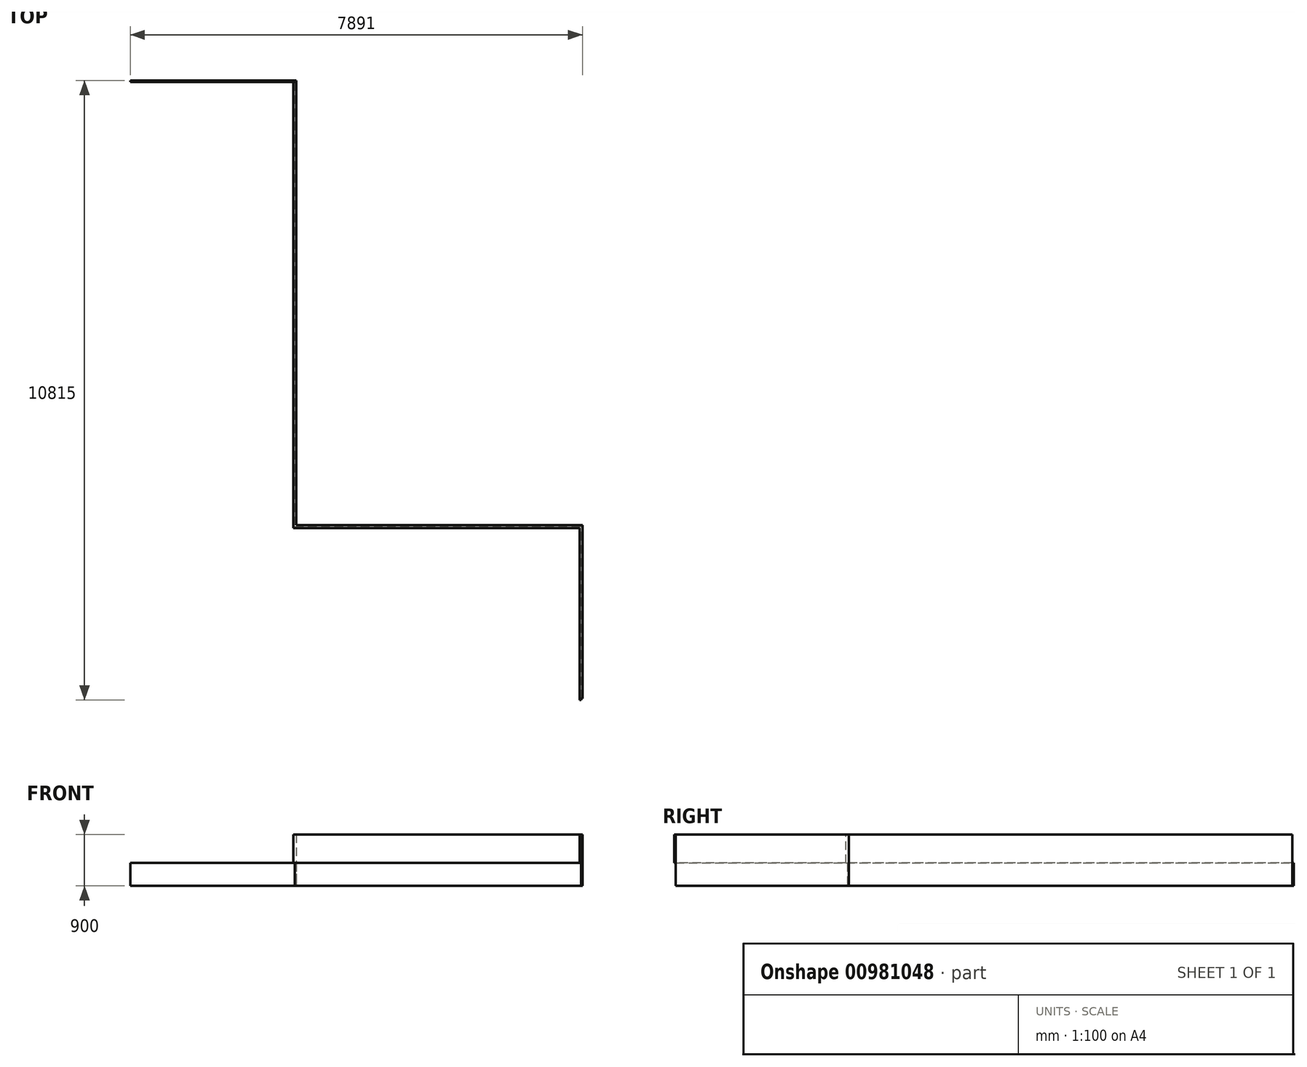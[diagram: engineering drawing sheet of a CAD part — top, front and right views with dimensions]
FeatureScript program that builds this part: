
annotation { "Feature Type Name" : "Feature", "Feature Type Description" : "" }
export const myFeature = defineFeature(function(context is Context, id is Id, definition is map)
    precondition{}
    {
        {
            var Q0;
            Q0=qCreatedBy(makeId("Front.planeOp"),FACE);
            var sketch = newSketch(context, id + "F0", { "sketchPlane" : qUnion([Q0])});
            skLineSegment(sketch, "E0.bottom", {"start": v(-6129.53, 738.4) * mm, "end": v(-1135.53, 738.4) * mm});
            skLineSegment(sketch, "E0.top", {"start": v(-6129.53, 338.4) * mm, "end": v(-1135.53, 338.4) * mm});
            skLineSegment(sketch, "E0.left", {"start": v(-6129.53, 738.4) * mm, "end": v(-6129.53, 338.4) * mm});
            skLineSegment(sketch, "E0.right", {"start": v(-1135.53, 738.4) * mm, "end": v(-1135.53, 338.4) * mm});
            skLineSegment(sketch, "E1.bottom", {"start": v(-6154.53, 738.4) * mm, "end": v(-1135.53, 738.4) * mm});
            skLineSegment(sketch, "E1.top", {"start": v(-6154.53, 1238.4) * mm, "end": v(-1135.53, 1238.4) * mm});
            skLineSegment(sketch, "E1.left", {"start": v(-6154.53, 738.4) * mm, "end": v(-6154.53, 1238.4) * mm});
            skLineSegment(sketch, "E1.right", {"start": v(-1135.53, 738.4) * mm, "end": v(-1135.53, 1238.4) * mm});
            skSolve(sketch);
        }
        {
            var Q0;
            Q0=makeQuery(id+"F0.imprint","IMPRINT",FACE,{"disambiguationData":[TD([[makeQuery(id+"F0.imprint","IMPRINT",EDGE,{"derivedFrom":sQuery(id+"F0.wireOp",EDGE,"E0.bottom")}),1.0]])]});
            extrude(context, id + "F1", {"entities" : qUnion([Q0]), "depth" : 25 * mm, "offsetDistance" : 25 * mm});
        }
        {
            var Q0;
            Q0=makeQuery(id+"F0.imprint","IMPRINT",FACE,{"disambiguationData":[TD([[makeQuery(id+"F0.imprint","IMPRINT",EDGE,{"derivedFrom":sQuery(id+"F0.wireOp",EDGE,"E0.bottom")}),-1.0]])]});
            var Q1;
            Q1=makeQuery(id+"F0.imprint","IMPRINT",FACE,{"disambiguationData":[TD([[makeQuery(id+"F0.imprint","IMPRINT",EDGE,{"derivedFrom":sQuery(id+"F0.wireOp",EDGE,"E0.bottom")}),1.0]])]});
            extrude(context, id + "F2", {"entities" : qUnion([Q0, Q1]), "operationType" : NewBodyOperationType.ADD, "oppositeDirection" : true, "depth" : 25 * mm, "offsetDistance" : 25 * mm});
        }
        {
            var Q0;
            {var subQ0=sQuery(id+"F0.wireOp",EDGE,"E1.right");Q0=makeQuery(id+"F2.boolean.opBoolean","MERGE",FACE,{"derivedFrom":[makeQuery(id+"F1.opExtrude","SWEPT_FACE",FACE,{"disambiguationData":[OSD([subQ0])]}),makeQuery(id+"F2.opExtrude","SWEPT_FACE",FACE,{"disambiguationData":[OSD([sQuery(id+"F0.wireOp",EDGE,"E0.right"),subQ0])]})]});}
            var sketch = newSketch(context, id + "F3", { "sketchPlane" : qUnion([Q0])});
            skLineSegment(sketch, "E2.bottom", {"start": v(25, 338.4) * mm, "end": v(-3003, 338.4) * mm});
            skLineSegment(sketch, "E2.top", {"start": v(25, 1238.4) * mm, "end": v(-3003, 1238.4) * mm});
            skLineSegment(sketch, "E2.left", {"start": v(25, 338.4) * mm, "end": v(25, 1238.4) * mm});
            skLineSegment(sketch, "E2.right", {"start": v(-3003, 338.4) * mm, "end": v(-3003, 1238.4) * mm});
            skLineSegment(sketch, "E3.bottom", {"start": v(-25, 738.4) * mm, "end": v(-3028, 738.4) * mm});
            skLineSegment(sketch, "E3.top", {"start": v(-25, 1238.4) * mm, "end": v(-3028, 1238.4) * mm});
            skLineSegment(sketch, "E3.left", {"start": v(-25, 738.4) * mm, "end": v(-25, 1238.4) * mm});
            skLineSegment(sketch, "E3.right", {"start": v(-3028, 738.4) * mm, "end": v(-3028, 1238.4) * mm});
            skSolve(sketch);
        }
        {
            var Q0;
            {var subQ5=sQuery(id+"F3.wireOp",EDGE,"E3.left");Q0=makeQuery(id+"F3.imprint","IMPRINT",FACE,{"disambiguationData":[TD([[makeQuery(id+"F3.imprint","IMPRINT",EDGE,{"derivedFrom":subQ5}),1.0]])]});}
            var Q1;
            {var subQ5=sQuery(id+"F3.wireOp",EDGE,"E3.right");Q1=makeQuery(id+"F3.imprint","IMPRINT",FACE,{"disambiguationData":[TD([[makeQuery(id+"F3.imprint","IMPRINT",EDGE,{"derivedFrom":subQ5}),-1.0]])]});}
            extrude(context, id + "F4", {"entities" : qUnion([Q0, Q1]), "operationType" : NewBodyOperationType.ADD, "oppositeDirection" : true, "depth" : 25 * mm, "offsetDistance" : 25 * mm});
        }
        {
            var Q0;
            {var subQ5=sQuery(id+"F3.wireOp",EDGE,"E3.left");Q0=makeQuery(id+"F3.imprint","IMPRINT",FACE,{"disambiguationData":[TD([[makeQuery(id+"F3.imprint","IMPRINT",EDGE,{"derivedFrom":subQ5}),1.0]])]});}
            var Q1;
            {var subQ0=sQuery(id+"F0.wireOp",EDGE,"E1.right");var subQ1=sQuery(id+"F0.wireOp",EDGE,"E0.right");var subQ8=makeQuery(id+"F2.opExtrude","CAP_EDGE",EDGE,{"disambiguationData":[OSD([subQ1,subQ0])],"isStart":true});Q1=makeQuery(id+"F3.imprint","IMPRINT",FACE,{"disambiguationData":[TD([[makeQuery(id+"F3.imprint","IMPRINT",EDGE,{"derivedFrom":subQ8}),-1.0]])]});}
            var Q2;
            Q2=makeQuery(id+"F3.imprint","IMPRINT",FACE,{"disambiguationData":[TD([[makeQuery(id+"F3.imprint","IMPRINT",EDGE,{"derivedFrom":sQuery(id+"F3.wireOp",EDGE,"E2.top")}),-1.0]])]});
            extrude(context, id + "F5", {"entities" : qUnion([Q0, Q1, Q2]), "operationType" : NewBodyOperationType.ADD, "depth" : 25 * mm, "offsetDistance" : 25 * mm});
        }
        {
            var Q0;
            Q0=makeQuery(id+"F2.opExtrude","SWEPT_FACE",FACE,{"disambiguationData":[OSD([sQuery(id+"F0.wireOp",EDGE,"E0.left")])]});
            var sketch = newSketch(context, id + "F6", { "sketchPlane" : qUnion([Q0])});
            skLineSegment(sketch, "E4.bottom", {"start": v(-25, 1238.4) * mm, "end": v(-7762, 1238.4) * mm});
            skLineSegment(sketch, "E4.top", {"start": v(-25, 338.4) * mm, "end": v(-7762, 338.4) * mm});
            skLineSegment(sketch, "E4.left", {"start": v(-25, 1238.4) * mm, "end": v(-25, 338.4) * mm});
            skLineSegment(sketch, "E4.right", {"start": v(-7762, 1238.4) * mm, "end": v(-7762, 338.4) * mm});
            skLineSegment(sketch, "E5.bottom", {"start": v(-25, 738.4) * mm, "end": v(-7762, 738.4) * mm});
            skLineSegment(sketch, "E5.left", {"start": v(-25, 738.4) * mm, "end": v(-25, 1238.4) * mm});
            skLineSegment(sketch, "E5.right", {"start": v(-7762, 738.4) * mm, "end": v(-7762, 1238.4) * mm});
            skSolve(sketch);
        }
        {
            var Q0;
            Q0=makeQuery(id+"F6.imprint","IMPRINT",FACE,{"disambiguationData":[TD([[makeQuery(id+"F6.imprint","IMPRINT",EDGE,{"derivedFrom":sQuery(id+"F6.wireOp",EDGE,"E5.bottom")}),-1.0]])]});
            var Q1;
            Q1=makeQuery(id+"F6.imprint","IMPRINT",FACE,{"disambiguationData":[TD([[makeQuery(id+"F6.imprint","IMPRINT",EDGE,{"derivedFrom":sQuery(id+"F6.wireOp",EDGE,"E4.top")}),-1.0]])]});
            extrude(context, id + "F7", {"entities" : qUnion([Q0, Q1]), "operationType" : NewBodyOperationType.ADD, "oppositeDirection" : true, "depth" : 25 * mm, "offsetDistance" : 25 * mm});
        }
        {
            var Q0;
            Q0=makeQuery(id+"F6.imprint","IMPRINT",FACE,{"disambiguationData":[TD([[makeQuery(id+"F6.imprint","IMPRINT",EDGE,{"derivedFrom":sQuery(id+"F6.wireOp",EDGE,"E5.bottom")}),-1.0]])]});
            extrude(context, id + "F8", {"entities" : qUnion([Q0]), "operationType" : NewBodyOperationType.ADD, "depth" : 25 * mm, "offsetDistance" : 25 * mm});
        }
        {
            var Q0;
            {var subQ0=sQuery(id+"F6.wireOp",EDGE,"E5.right");Q0=makeQuery(id+"F8.boolean.opBoolean","MERGE",FACE,{"derivedFrom":[makeQuery(id+"F7.opExtrude","SWEPT_FACE",FACE,{"disambiguationData":[OSD([sQuery(id+"F6.wireOp",EDGE,"E4.right"),subQ0])]}),makeQuery(id+"F8.opExtrude","SWEPT_FACE",FACE,{"disambiguationData":[OSD([subQ0])]})]});}
            var sketch = newSketch(context, id + "F9", { "sketchPlane" : qUnion([Q0])});
            skLineSegment(sketch, "E6.bottom", {"start": v(6129.53, 338.4) * mm, "end": v(9001.53, 338.4) * mm});
            skLineSegment(sketch, "E6.top", {"start": v(6129.53, 738.4) * mm, "end": v(9001.53, 738.4) * mm});
            skLineSegment(sketch, "E6.left", {"start": v(6129.53, 338.4) * mm, "end": v(6129.53, 738.4) * mm});
            skLineSegment(sketch, "E6.right", {"start": v(9001.53, 338.4) * mm, "end": v(9001.53, 738.4) * mm});
            skLineSegment(sketch, "E7.bottom", {"start": v(6129.53, 738.4) * mm, "end": v(6104.53, 738.4) * mm});
            skLineSegment(sketch, "E7.top", {"start": v(6129.53, 338.4) * mm, "end": v(6104.53, 338.4) * mm});
            skLineSegment(sketch, "E7.left", {"start": v(6129.53, 738.4) * mm, "end": v(6129.53, 338.4) * mm});
            skLineSegment(sketch, "E7.right", {"start": v(6104.53, 738.4) * mm, "end": v(6104.53, 338.4) * mm});
            skSolve(sketch);
        }
        {
            var Q0;
            Q0=makeQuery(id+"F9.imprint","IMPRINT",FACE,{"disambiguationData":[TD([[makeQuery(id+"F9.imprint","IMPRINT",EDGE,{"derivedFrom":sQuery(id+"F9.wireOp",EDGE,"E6.bottom")}),1.0]])]});
            var Q1;
            Q1=makeQuery(id+"F9.imprint","IMPRINT",FACE,{"disambiguationData":[TD([[makeQuery(id+"F9.imprint","IMPRINT",EDGE,{"derivedFrom":sQuery(id+"F9.wireOp",EDGE,"E7.bottom")}),1.0]])]});
            extrude(context, id + "F10", {"entities" : qUnion([Q0, Q1]), "depth" : 25 * mm, "offsetDistance" : 25 * mm});
        }
    });
